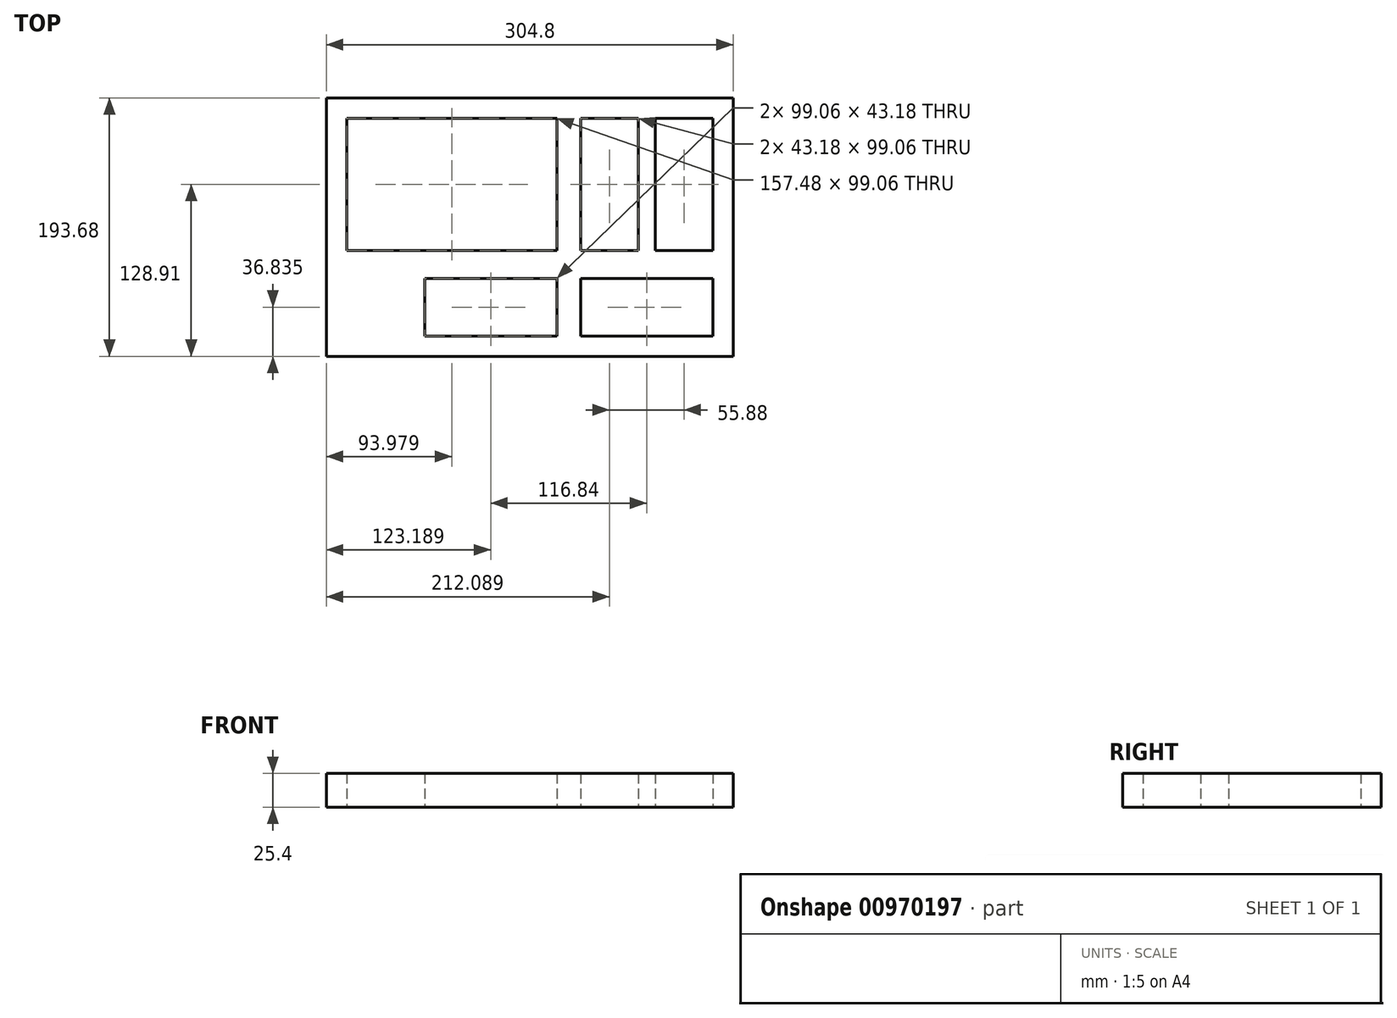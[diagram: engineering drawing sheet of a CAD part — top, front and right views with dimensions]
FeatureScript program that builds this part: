
annotation { "Feature Type Name" : "Feature", "Feature Type Description" : "" }
export const myFeature = defineFeature(function(context is Context, id is Id, definition is map)
    precondition{}
    {
        {
            var Q0;
            Q0=qCreatedBy(makeId("Top.planeOp"),FACE);
            var sketch = newSketch(context, id + "F0", { "sketchPlane" : qUnion([Q0])});
            skLineSegment(sketch, "E0.bottom", {"start": v(-47.2, 144.73) * mm, "end": v(257.6, 144.73) * mm});
            skLineSegment(sketch, "E0.top", {"start": v(-47.2, -48.95) * mm, "end": v(257.6, -48.95) * mm});
            skLineSegment(sketch, "E0.left", {"start": v(-47.2, 144.73) * mm, "end": v(-47.2, -48.95) * mm});
            skLineSegment(sketch, "E0.right", {"start": v(257.6, 144.73) * mm, "end": v(257.6, -48.95) * mm});
            skLineSegment(sketch, "E1.bottom", {"start": v(-31.96, 129.49) * mm, "end": v(125.52, 129.49) * mm});
            skLineSegment(sketch, "E1.top", {"start": v(-31.96, 30.43) * mm, "end": v(125.52, 30.43) * mm});
            skLineSegment(sketch, "E1.left", {"start": v(-31.96, 129.49) * mm, "end": v(-31.96, 30.43) * mm});
            skLineSegment(sketch, "E1.right", {"start": v(125.52, 129.49) * mm, "end": v(125.52, 30.43) * mm});
            skLineSegment(sketch, "E2.bottom", {"start": v(143.3, 129.49) * mm, "end": v(186.48, 129.49) * mm});
            skLineSegment(sketch, "E2.top", {"start": v(143.3, 30.43) * mm, "end": v(186.48, 30.43) * mm});
            skLineSegment(sketch, "E2.left", {"start": v(143.3, 129.49) * mm, "end": v(143.3, 30.43) * mm});
            skLineSegment(sketch, "E2.right", {"start": v(186.48, 129.49) * mm, "end": v(186.48, 30.43) * mm});
            skLineSegment(sketch, "E3.bottom", {"start": v(199.18, 129.49) * mm, "end": v(242.36, 129.49) * mm});
            skLineSegment(sketch, "E3.top", {"start": v(199.18, 30.43) * mm, "end": v(242.36, 30.43) * mm});
            skLineSegment(sketch, "E3.left", {"start": v(199.18, 129.49) * mm, "end": v(199.18, 30.43) * mm});
            skLineSegment(sketch, "E3.right", {"start": v(242.36, 129.49) * mm, "end": v(242.36, 30.43) * mm});
            skLineSegment(sketch, "E4.bottom", {"start": v(143.3, 9.47) * mm, "end": v(242.36, 9.47) * mm});
            skLineSegment(sketch, "E4.top", {"start": v(143.3, -33.7) * mm, "end": v(242.36, -33.7) * mm});
            skLineSegment(sketch, "E4.left", {"start": v(143.3, 9.47) * mm, "end": v(143.3, -33.7) * mm});
            skLineSegment(sketch, "E4.right", {"start": v(242.36, 9.47) * mm, "end": v(242.36, -33.7) * mm});
            skLineSegment(sketch, "E5.bottom", {"start": v(26.46, 9.47) * mm, "end": v(125.52, 9.47) * mm});
            skLineSegment(sketch, "E5.top", {"start": v(26.46, -33.7) * mm, "end": v(125.52, -33.7) * mm});
            skLineSegment(sketch, "E5.left", {"start": v(26.46, 9.47) * mm, "end": v(26.46, -33.7) * mm});
            skLineSegment(sketch, "E5.right", {"start": v(125.52, 9.47) * mm, "end": v(125.52, -33.7) * mm});
            skSolve(sketch);
        }
        {
            var Q0;
            Q0=makeQuery(id+"F0.imprint","IMPRINT",FACE,{"disambiguationData":[TD([[makeQuery(id+"F0.imprint","IMPRINT",EDGE,{"derivedFrom":sQuery(id+"F0.wireOp",EDGE,"E0.bottom")}),-1.0]])]});
            extrude(context, id + "F1", {"entities" : qUnion([Q0]), "depth" : 25.4 * mm, "offsetDistance" : 25.4 * mm});
        }
    });
